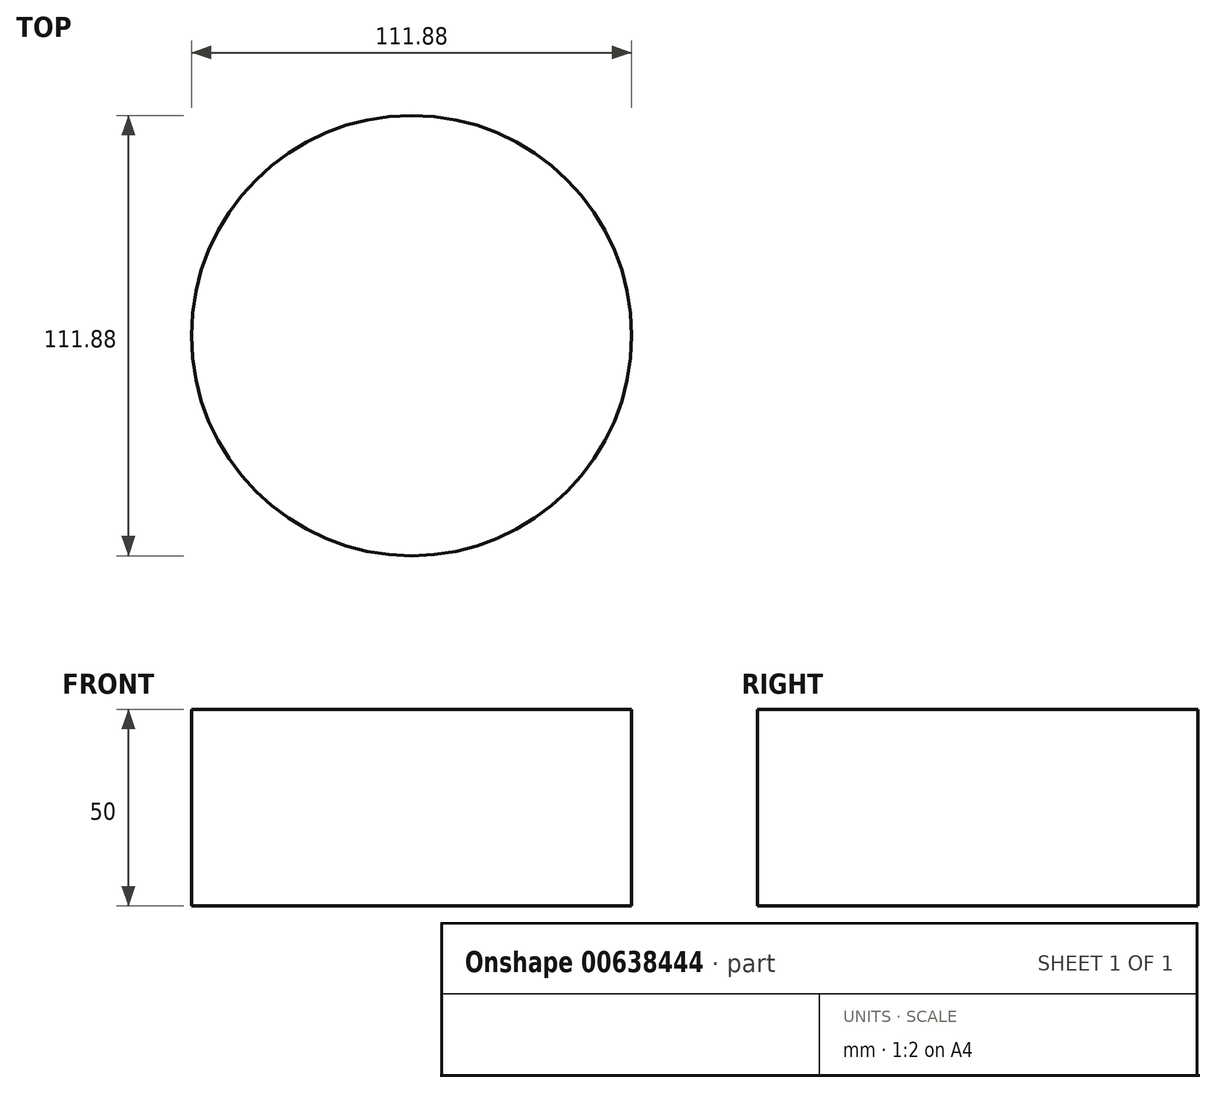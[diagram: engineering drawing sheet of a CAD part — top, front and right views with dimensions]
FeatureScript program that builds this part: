
annotation { "Feature Type Name" : "Feature", "Feature Type Description" : "" }
export const myFeature = defineFeature(function(context is Context, id is Id, definition is map)
    precondition{}
    {
        {
            var Q0;
            Q0=qCreatedBy(makeId("Top.planeOp"),FACE);
            var sketch = newSketch(context, id + "F0", { "sketchPlane" : qUnion([Q0])});
            skCircle(sketch, "E0", {"center": v(0, 0) * mm, "radius": 55.94 * mm});
            skSolve(sketch);
        }
        {
            var Q0;
            Q0 = qSketchRegion(id + "F0", true);
            extrude(context, id + "F1", {"entities" : qUnion([Q0]), "depth" : 50 * mm, "offsetDistance" : 25 * mm});
        }
    });
